# Revit family: Domotics-DomesticRanges-GEWISS-SYSTEM_COMMAND-DIMMER_ROTATING
name_source: partatom
category: Apparecchi elettrici
revit_build: Autodesk Revit 2016 (Build: 20161004_0715(x64)
units: mm (PartAtom-declared; Revit-internal decimal feet)

## family parameters
Condiviso = Sì
Host = Superficie
Mantenere orientamento annotazione = Sì
Punto di calcolo locali = Sì
Quota connettore circolare = Usa diametro
Taglio con vuoti quando caricato = Sì
Tipo di parte = Normale

## types (6) — shared parameters
Carico apparente = 0 VA
Catalogue = DOMOTICS
Catalogue Range = SYSTEM - DOMESTIC RANGE
Command = Rotary
Control = Rotary
Description. = Rotary dimmer
Electrocod = 0130
IDF = 4e647ec0-afb7-4243-b30c-ae0389bc0b33
IDT = cd208314-872c-4e47-a50d-a4c5fc02c05e
Immagine tipo = GW21811.jpg
N. poli = 1
No. SYSTEM modules = 1
Produttore = GEWISS S.p.A.
Prospetto di default = 1219 mm
SEO = Dimmer
Supply voltage = 230V - 50 / 60 Hz
TIPO = System Dimmer Pulsante Rotativo_GENERICO : nero
Technical sheet = https://www.gewiss.com
Tipo simbolo = PULSANTI : DIMMMANOPDEV
URL = https://www.gewiss.com
Version file RFA = 19.4
Volt = 230 V

## per-type parameters (varying)
| type | Colour | Descrizione | EAN code | Inductive load | Inductive load 230V ac | Load type | Modello | Resistive load | Resistive load 230V ac |
| GW20811 - Elec.dimmer rot.2way 230V 100-500W white | White | ELEC.DIMMER ROT.2WAY 230V 100-500W SY/WT | 8011564054875 | 100-500 VA | 100-500 VA | Resistive/Inductive | GW20811 | 100-500 W | 100-500 W |
| GW21802 - Elec.dimmer rot.230V 100-500W black | Black | ELEC.DIMMER ROT.230V 100-500W SY/BK | 8011564129320 |  |  | Resistive | GW21802 | 100-500 W | 100-500 W |
| GW20803 - Elec.dimmer rot.230V 100-900W white | White | ELEC.DIMMER ROT.230V 100-900W SY/WT | 8011564001190 | 40-300 VA | 40-300 VA | Resistive/Inductive | GW20803 | 100-900 W | 100-900 W |
| GW21803 - Elec.dimmer rot.230V 100-900W black | Black | ELEC.DIMMER ROT.230V 100-900W SY/BK | 8011564129344 | 40-300 VA | 40-300 VA | Resistive/Inductive | GW21803 | 100-900 W | 100-900 W |
| GW20802 - Elec.dimmer rot.230V 100-500W white | White | ELEC.DIMMER ROT.230V 100-500W SY/WT | 8011564001183 |  |  | Resistive | GW20802 | 100-500 W | 100-500 W |
| GW21811 - Elec.dimmer rot.2way 230V 100-500W black | Black | ELEC.DIMMER ROT.2WAY 230V 100-500W SY/BK | 8011564129351 | 100-500 VA | 100-500 VA | Resistive/Inductive | GW21811 | 100-500 W | 100-500 W |

## geometry (parser evidence)
native form markers: Sweep x1
no freeform markers — native parametric forms only
